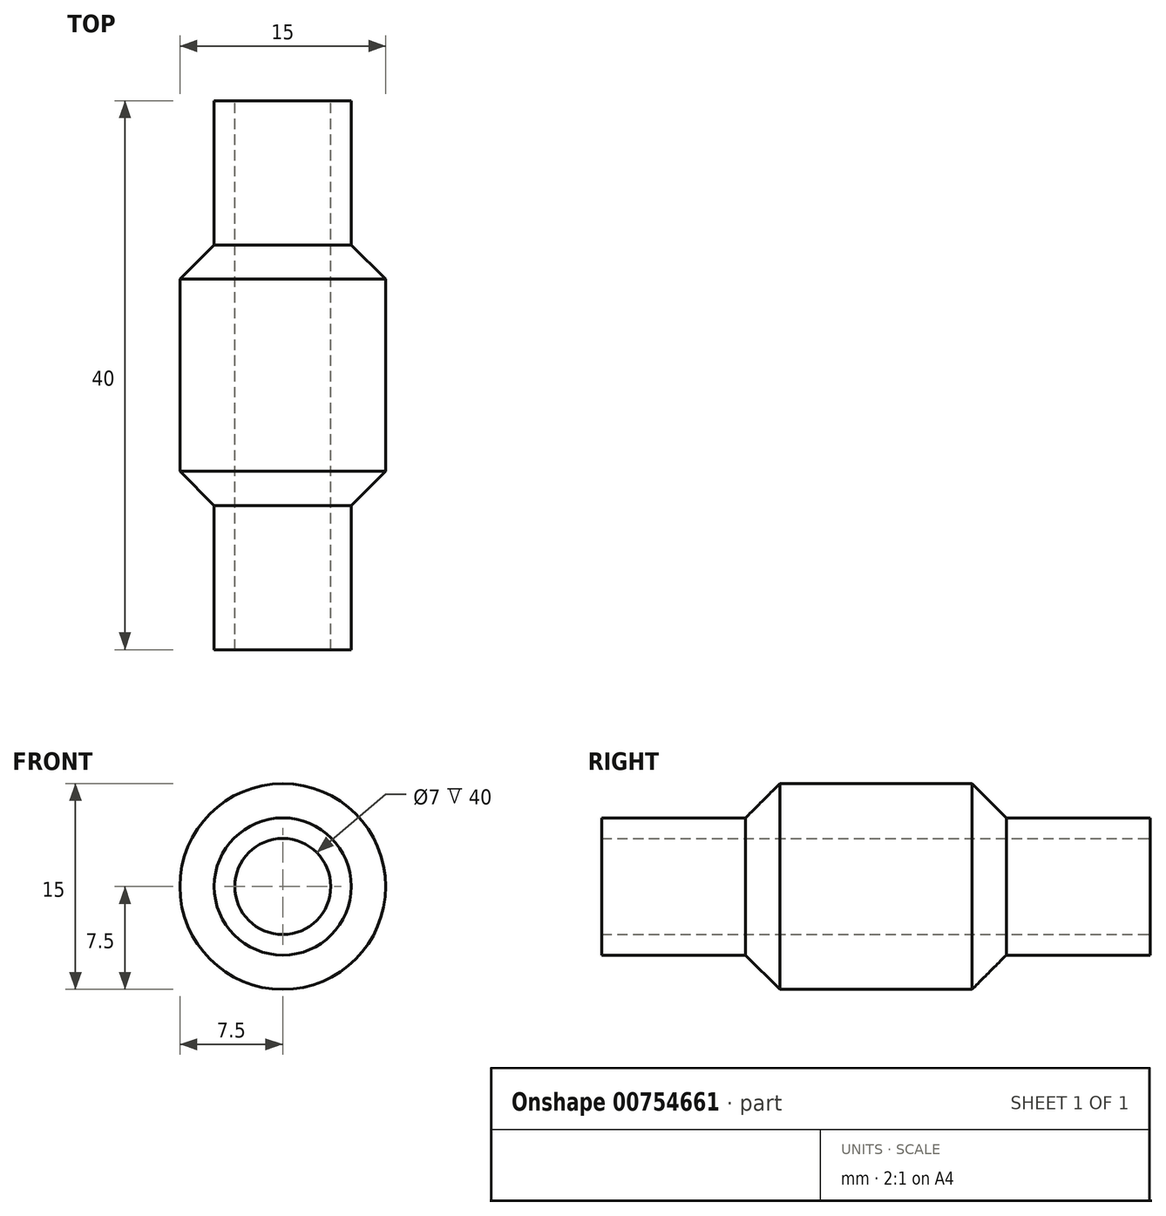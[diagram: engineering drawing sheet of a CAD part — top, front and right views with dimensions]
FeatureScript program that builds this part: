
annotation { "Feature Type Name" : "Feature", "Feature Type Description" : "" }
export const myFeature = defineFeature(function(context is Context, id is Id, definition is map)
    precondition{}
    {
        {
            var Q0;
            Q0=qCreatedBy(makeId("Front.planeOp"),FACE);
            var sketch = newSketch(context, id + "F0", { "sketchPlane" : qUnion([Q0])});
            skCircle(sketch, "E0", {"center": v(0, 0) * mm, "radius": 5 * mm});
            skCircle(sketch, "E1", {"center": v(0, 0) * mm, "radius": 3.5 * mm});
            skSolve(sketch);
        }
        {
            var Q0;
            Q0=makeQuery(id+"F0.imprint","IMPRINT",FACE,{"disambiguationData":[TD([[makeQuery(id+"F0.imprint","IMPRINT",EDGE,{"derivedFrom":sQuery(id+"F0.wireOp",EDGE,"E0")}),1.0]])]});
            extrude(context, id + "F1", {"entities" : qUnion([Q0]), "depth" : 10 * mm, "offsetDistance" : 25 * mm});
        }
        {
            var Q0;
            Q0=makeQuery(id+"F1.opExtrude","CAP_FACE",FACE,{"disambiguationData":[OSD([sQuery(id+"F0.wireOp",EDGE,"E0"),sQuery(id+"F0.wireOp",EDGE,"E1")])],"isStart":true});
            var sketch = newSketch(context, id + "F2", { "sketchPlane" : qUnion([Q0])});
            skCircle(sketch, "E2", {"center": v(0, 0) * mm, "radius": 7.5 * mm});
            skSolve(sketch);
        }
        {
            var Q0;
            Q0=makeQuery(id+"F2.imprint","IMPRINT",FACE,{"disambiguationData":[TD([[makeQuery(id+"F2.imprint","IMPRINT",EDGE,{"derivedFrom":sQuery(id+"F2.wireOp",EDGE,"E2")}),1.0]])]});
            var Q1;
            Q1=makeQuery(id+"F2.imprint","IMPRINT",FACE,{"disambiguationData":[TD([[makeQuery(id+"F2.imprint","IMPRINT",EDGE,{"derivedFrom":makeQuery(id+"F1.opExtrude","CAP_EDGE",EDGE,{"disambiguationData":[OSD([sQuery(id+"F0.wireOp",EDGE,"E0")])],"isStart":true})}),-1.0]])]});
            extrude(context, id + "F3", {"entities" : qUnion([Q0, Q1]), "operationType" : NewBodyOperationType.ADD, "depth" : 10 * mm, "offsetDistance" : 25 * mm});
        }
        {
            var Q0;
            Q0=makeQuery(id+"F1.opExtrude","SWEPT_BODY",BODY,{"disambiguationData":[OSD([sQuery(id+"F0.wireOp",EDGE,"E0"),sQuery(id+"F0.wireOp",EDGE,"E1")])]});
            var Q1;
            Q1=makeQuery(id+"F3.opExtrude","CAP_FACE",FACE,{"disambiguationData":[OSD([sQuery(id+"F0.wireOp",EDGE,"E1"),sQuery(id+"F2.wireOp",EDGE,"E2")])],"isStart":false});
            mirror(context, id + "F4", {"operationType" : NewBodyOperationType.ADD, "entities" : qUnion([Q0]), "mirrorPlane" : qUnion([Q1])});
        }
        {
            var Q0;
            Q0=makeQuery(id+"F4.opPattern","COPY",EDGE,{"derivedFrom":makeQuery(id+"F3.opExtrude","CAP_EDGE",EDGE,{"disambiguationData":[OSD([sQuery(id+"F2.wireOp",EDGE,"E2")])],"isStart":true}),"instanceName":"1"});
            var Q1;
            Q1=makeQuery(id+"F3.opExtrude","CAP_EDGE",EDGE,{"disambiguationData":[OSD([sQuery(id+"F2.wireOp",EDGE,"E2")])],"isStart":true});
            chamfer(context, id + "F5", {"entities" : qUnion([Q0, Q1]), "width" : 3 * mm, "tangentPropagation" : true});
        }
    });
